# Revit family: Legrand Export Snap on Mini Columns
name_source: partatom
category: Installations électriques
units: mm (PartAtom-declared; Revit-internal decimal feet)

## family parameters
Basée sur le plan de construction = Non
Conserver l'orientation des annotations = Non
Cote de connecteur circulaire = Utiliser le diamètre
Couper avec des vides une fois chargée = Non
Partagée = Non
Point de calcul de pièce = Non
Toujours verticalement = Oui
Type d'élément = Normal

## types (19) — shared parameters
Fabricant = LEGRAND
Standard = Snap-on-ON
zero-valued in all types: Elévation par défaut

## per-type parameters (varying)
| type | 1 CPT | 2 CPT | 4 CPT | Black | Column stand | Description | Finishing | H1 | HC | Largeur | Longueur | Main Material | Matériau couvercle | Matériaux corps | Modèle | Number of compartments | Séparateur |
| Column 1 cpt CV45 0,30M White | Oui | Non | Non | Non | Movable feet : Foot for mini Column White | mini Column direct clipping 1 compartment 0,30m White | White | 300 mm | 260 mm  [stored 0.853018 ft] | 75 mm  [stored 0.246063 ft] | 82 mm | Aluminum | Legrand - Plastique blanc | Legrand - Aluminium blanc | LG-653000 | 1 compartment | 35 mm |
| Column 1 cpt CV45 0,30M Alu | Oui | Non | Non | Non | Movable feet : Foot for mini Column Alu | mini Column direct clipping 1 compartment 0,30m Aluminium | Aluminum | 300 mm | 260 mm  [stored 0.853018 ft] | 75 mm  [stored 0.246063 ft] | 82 mm | Aluminum | Legrand - Plastique gris | Legrand - Aluminium gris | LG-653001 | 1 compartment | 35 mm |
| Column 1 cpt CV45 0,30M Black | Oui | Non | Non | Oui | Shelf : Table for mini Column T1/2 | mini Column direct clipping 1 compartment 0,30m Black | Black | 300 mm | 260 mm  [stored 0.853018 ft] | 75 mm  [stored 0.246063 ft] | 82 mm | Aluminum | Legrand - Plastique noir | Legrand - Aluminium noir | LG-653002 | 1 compartment | 35 mm |
| Column 1 cpt CV45 0,68M White | Oui | Non | Non | Non | Movable feet : Foot for mini Column White | mini Column direct clipping 1 compartment 0,68m White | White | 680 mm  [stored 2.23097 ft] | 640 mm  [stored 2.09974 ft] | 75 mm  [stored 0.246063 ft] | 82 mm | Aluminum | Legrand - Plastique blanc | Legrand - Aluminium blanc | LG-653003 | 1 compartment | 35 mm |
| Column 1 cpt CV45 0,68M Alu | Oui | Non | Non | Non | Movable feet : Foot for mini Column Alu | mini Column direct clipping 1 compartment 0,68m Aluminium | Aluminum | 680 mm  [stored 2.23097 ft] | 640 mm  [stored 2.09974 ft] | 75 mm  [stored 0.246063 ft] | 82 mm | Aluminum | Legrand - Plastique gris | Legrand - Aluminium gris | LG-653004 | 1 compartment | 35 mm |
| Column 1 cpt CV45 0,68M Black | Oui | Non | Non | Oui | Shelf : Table for mini Column T1/2 | mini Column direct clipping 1 compartment 0,68m Black | Black | 680 mm  [stored 2.23097 ft] | 640 mm  [stored 2.09974 ft] | 75 mm  [stored 0.246063 ft] | 82 mm | Aluminum | Legrand - Plastique noir | Legrand - Aluminium noir | LG-653005 | 1 compartment | 35 mm |
| Column 2 cpts CV45 0,3M White | Non | Oui | Non | Non | Movable feet : Foot for mini Column White | mini Column direct clipping 2 compartments 0,30m White | White | 300 mm | 260 mm  [stored 0.853018 ft] | 75 mm  [stored 0.246063 ft] | 125 mm  [stored 0.410105 ft] | Plastic | Legrand - Plastique blanc | Legrand - Plastique blanc | LG-653020 | 2 compartments | 35 mm |
| Column 2 cpts CV45 0,3M Alu | Non | Oui | Non | Non | Movable feet : Foot for mini Column Alu | mini Column direct clipping 2 compartments 0,30m Aluminium | Aluminum | 300 mm | 260 mm  [stored 0.853018 ft] | 75 mm  [stored 0.246063 ft] | 125 mm  [stored 0.410105 ft] | Aluminum | Legrand - Plastique gris | Legrand - Aluminium gris | LG-653021 | 2 compartments | 35 mm |
| Column 2 cpts CV45 0,3M Black | Non | Oui | Non | Oui | Shelf : Table for mini Column T1/2 | mini Column direct clipping 2 compartments 0,30m Black | Black | 300 mm | 260 mm  [stored 0.853018 ft] | 75 mm  [stored 0.246063 ft] | 125 mm  [stored 0.410105 ft] | Aluminum | Legrand - Plastique noir | Legrand - Aluminium noir | LG-653022 | 2 compartments | 35 mm |
| Column 2 cpts 45 0,68M White | Non | Oui | Non | Non | Movable feet : Foot for mini Column White | mini Column direct clipping 2 compartments 0,68m White | White | 380 mm | 340 mm | 75 mm  [stored 0.246063 ft] | 125 mm  [stored 0.410105 ft] | Aluminum | Legrand - Plastique blanc | Legrand - Aluminium blanc | LG-653023 | 2 compartments | 35 mm |
| Column 2 cpts CV45 0,68M Alu | Non | Oui | Non | Non | Movable feet : Foot for mini Column Alu | mini Column direct clipping 2 compartments 0,68m Aluminium | Aluminum | 680 mm  [stored 2.23097 ft] | 640 mm  [stored 2.09974 ft] | 75 mm  [stored 0.246063 ft] | 125 mm  [stored 0.410105 ft] | Aluminum | Legrand - Plastique gris | Legrand - Aluminium gris | LG-653024 | 2 compartments | 35 mm |
| Column 2 cpts CV45 0,68M Black | Non | Oui | Non | Oui | Shelf : Table for mini Column T1/2 | mini Column direct clipping 2 compartments 0,68m Black | Black | 680 mm  [stored 2.23097 ft] | 640 mm  [stored 2.09974 ft] | 75 mm  [stored 0.246063 ft] | 125 mm  [stored 0.410105 ft] | Aluminum | Legrand - Plastique noir | Legrand - Aluminium noir | LG-653025 | 2 compartments | 35 mm |
| Column 4 cpts 45 0,30M White | Non | Non | Oui | Non | Movable feet : Foot for mini Column White | mini Column direct clipping 4 compartments 0,30m White | White | 300 mm | 260 mm  [stored 0.853018 ft] | 125 mm  [stored 0.410105 ft] | 125 mm  [stored 0.410105 ft] | Aluminum | Legrand - Plastique blanc | Legrand - Aluminium blanc | LG-653040 | 4 compartments | 125 mm  [stored 0.410105 ft] |
| Column 4 cpts CV45 0,30M Alu | Non | Non | Oui | Non | Movable feet : Foot for mini Column Alu | mini Column direct clipping 4 compartments 0,30m Aluminium | Aluminum | 300 mm | 260 mm  [stored 0.853018 ft] | 125 mm  [stored 0.410105 ft] | 125 mm  [stored 0.410105 ft] | Aluminum | Legrand - Plastique gris | Legrand - Aluminium gris | LG-653041 | 4 compartments | 125 mm  [stored 0.410105 ft] |
| Column 4 cpts CV45 0,30M Black | Non | Non | Oui | Oui | Shelf : Table for mini Column T1/2 | mini Column direct clipping 4 compartments 0,30m Black | Black | 300 mm | 260 mm  [stored 0.853018 ft] | 125 mm  [stored 0.410105 ft] | 125 mm  [stored 0.410105 ft] | Aluminum | Legrand - Plastique noir | Legrand - Aluminium noir | LG-653042 | 4 compartments | 125 mm  [stored 0.410105 ft] |
| Column 4 cpts CV45 0,68M Black | Non | Non | Oui | Oui | Shelf : Table for mini Column T1/2 | mini Column direct clipping 4 compartments 0,68m Black | Black | 680 mm  [stored 2.23097 ft] | 640 mm  [stored 2.09974 ft] | 125 mm  [stored 0.410105 ft] | 125 mm  [stored 0.410105 ft] | Aluminum | Legrand - Plastique noir | Legrand - Aluminium noir | LG-653045 | 4 compartments | 125 mm  [stored 0.410105 ft] |
| Column 4 cpts CV45 0,68M Alu | Non | Non | Oui | Non | Movable feet : Foot for mini Column Alu | mini Column direct clipping 4 compartments 0,68m Aluminium | Aluminum | 680 mm  [stored 2.23097 ft] | 640 mm  [stored 2.09974 ft] | 125 mm  [stored 0.410105 ft] | 125 mm  [stored 0.410105 ft] | Aluminum | Legrand - Plastique gris | Legrand - Aluminium gris | LG-653044 | 4 compartments | 125 mm  [stored 0.410105 ft] |
| Column 4 cpts 45 0,68M White | Non | Non | Oui | Non | Movable feet : Foot for mini Column White | mini Column direct clipping 4 compartments 0,68m White | White | 680 mm  [stored 2.23097 ft] | 640 mm  [stored 2.09974 ft] | 125 mm  [stored 0.410105 ft] | 125 mm  [stored 0.410105 ft] | Aluminum | Legrand - Plastique blanc | Legrand - Aluminium blanc | LG-653043 | 4 compartments | 125 mm  [stored 0.410105 ft] |
| Roll&Plug 2 cpts 0,68M White | Non | Oui | Non | Non | Movable feet : Foot for mini Column White | roll and plug 2 cpts 0,68m White table foot wheels 6pc+e fs dble usb 4m p cable | White | 680 mm  [stored 2.23097 ft] | 640 mm  [stored 2.09974 ft] | 75 mm  [stored 0.246063 ft] | 125 mm  [stored 0.410105 ft] | Aluminum | Legrand - Plastique blanc | Legrand - Aluminium blanc | LG-653029 | 2 compartments | 35 mm |

note: [stored X ft] marks values corroborated as IEEE doubles in the binary element streams (Revit-internal decimal feet)
